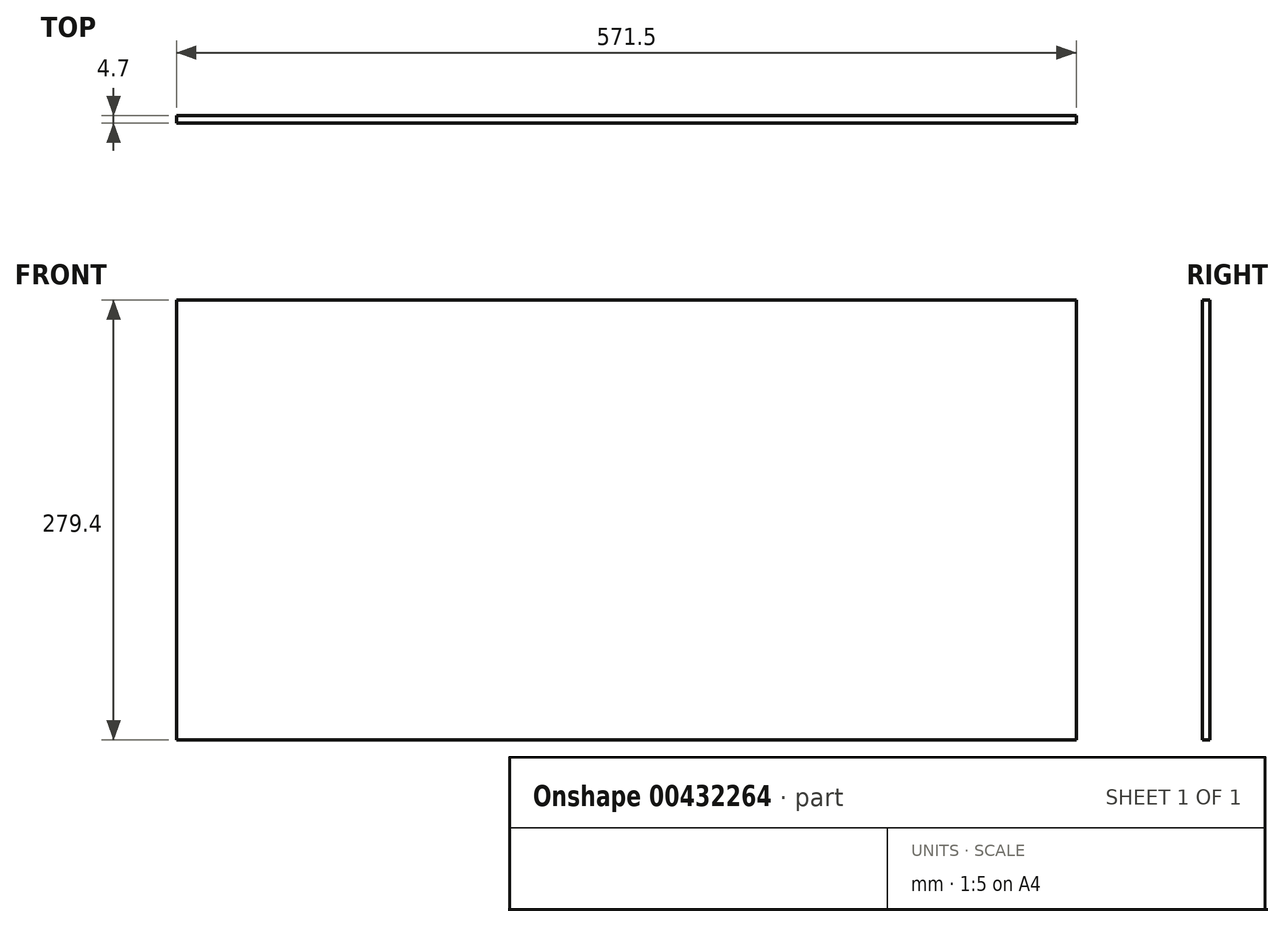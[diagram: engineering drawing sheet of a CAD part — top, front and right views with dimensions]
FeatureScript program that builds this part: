
annotation { "Feature Type Name" : "Feature", "Feature Type Description" : "" }
export const myFeature = defineFeature(function(context is Context, id is Id, definition is map)
    precondition{}
    {
        {
            var Q0;
            Q0=qCreatedBy(makeId("Front.planeOp"),FACE);
            var sketch = newSketch(context, id + "F0", { "sketchPlane" : qUnion([Q0])});
            skLineSegment(sketch, "E0.bottom", {"start": v(-285.75, 139.7) * mm, "end": v(285.75, 139.7) * mm});
            skLineSegment(sketch, "E0.top", {"start": v(-285.75, -139.7) * mm, "end": v(285.75, -139.7) * mm});
            skLineSegment(sketch, "E0.left", {"start": v(-285.75, 139.7) * mm, "end": v(-285.75, -139.7) * mm});
            skLineSegment(sketch, "E0.right", {"start": v(285.75, 139.7) * mm, "end": v(285.75, -139.7) * mm});
            skPoint(sketch, "E0.middle", {"position": v(0, 0) * mm});
            skSolve(sketch);
        }
        {
            var Q0;
            Q0 = qSketchRegion(id + "F0", true);
            extrude(context, id + "F1", {"entities" : qUnion([Q0]), "depth" : 4.7 * mm, "offsetDistance" : 25.4 * mm});
        }
    });
